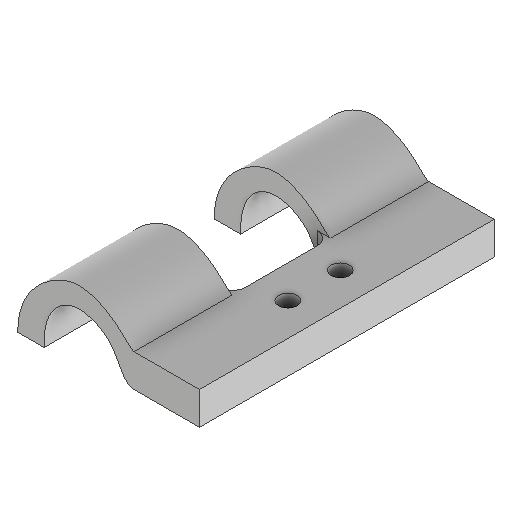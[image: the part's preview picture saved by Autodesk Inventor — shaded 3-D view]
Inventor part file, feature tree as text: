
AUTODESK INVENTOR PART (.ipt)
format: ipt  version: 2024.1 (Build 281209000, 209)  size: 179,712 bytes
history: native  units: mm
features: reference x4, extrude x3, sketch x3, projected_geometry x2, other x2, fillet x1
ambient origin geometry x8: Origin, YZ Plane, XZ Plane, XY Plane, X Axis, Y Axis, Z Axis, Center Point
bodies: Volumenkörper1 (feature_tree)
feature tree (15):
  extrude  "Extrusion1"  Depth=10.0mm
  extrude  "Extrusion2"  Depth=5.0mm TaperAngle=0.0deg
  extrude  "Extrusion3"  TaperAngle=0.0deg  [1 undecoded]
  fillet  "Rundung1"  Radius=2.0mm
  sketch  "Skizze1"  dims[d0=10.0mm d1=45.0mm]
  reference  "Referenz1"
  reference  "Referenz2"
  reference  "Referenz3"
  reference  "Referenz4"
  sketch  "Skizze2"  dims[d2=5.0mm d3=0.0mm d4=5.0mm d5=0.0mm]
  projected_geometry  "Projizierte Kontur1"
  sketch  "Skizze3"  dims[d6=15.0mm d7=0.0mm d8=0.0mm d9=2.0mm]
  projected_geometry  "Projizierte Kontur2"
  other  "Assembly_Planktoscope_Uc2version_wormdrive_V3.iam"
  other  "60_Planktoscope_Sampleholder:1"
note: 1 required parameter value undecoded (feature->parameter linkage not recoverable at this tier; creation-order binding heuristic only, values carry confidence <= 0.55)
